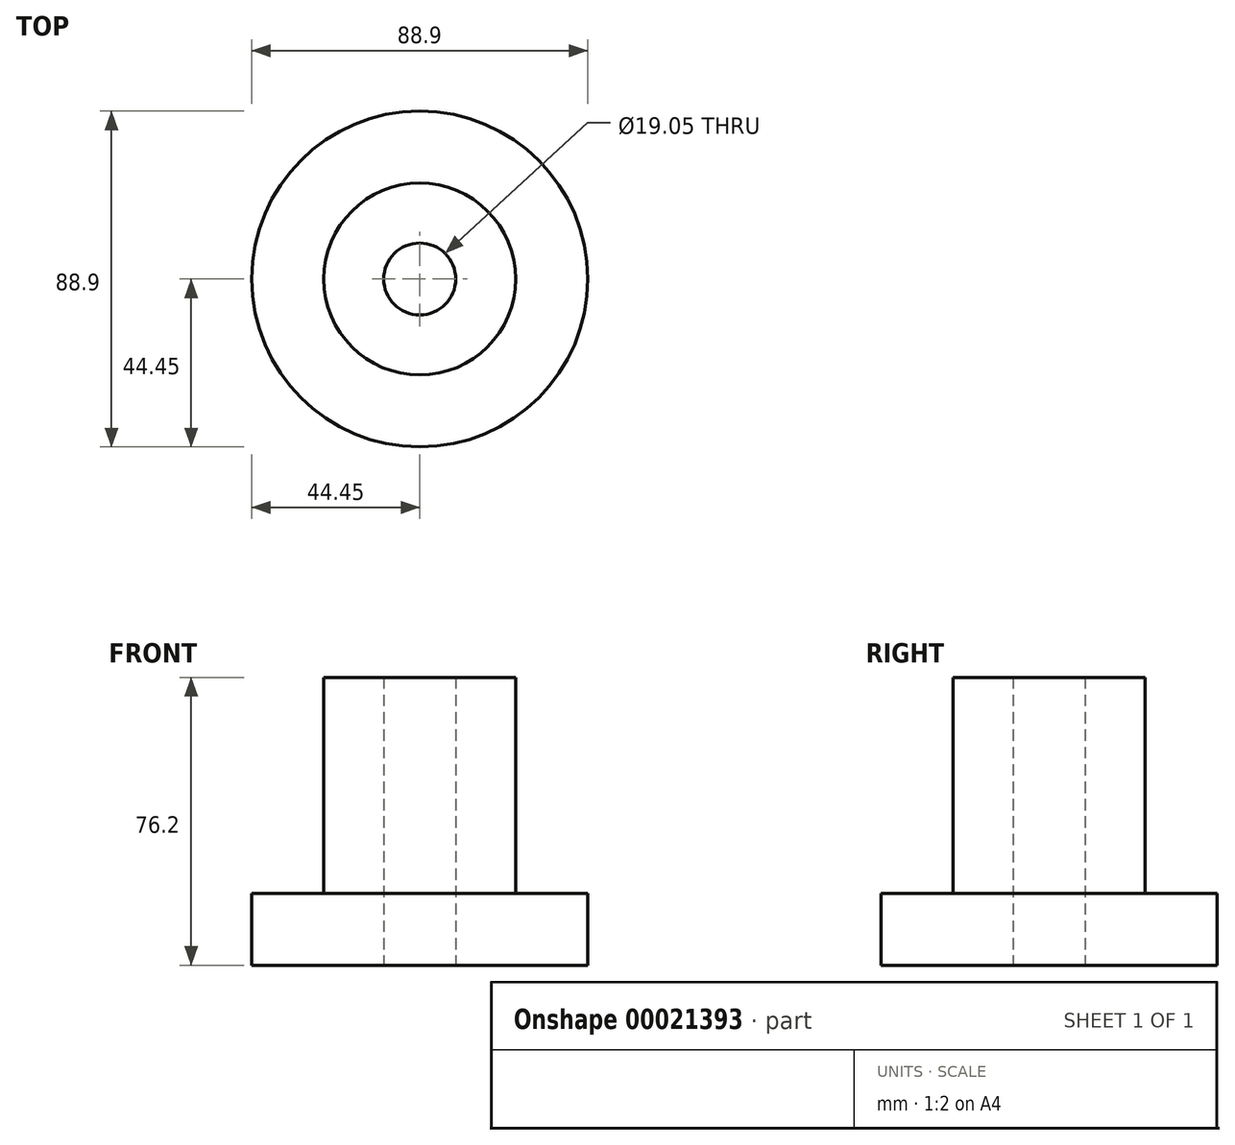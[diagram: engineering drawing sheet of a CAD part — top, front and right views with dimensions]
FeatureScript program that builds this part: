
annotation { "Feature Type Name" : "Feature", "Feature Type Description" : "" }
export const myFeature = defineFeature(function(context is Context, id is Id, definition is map)
    precondition{}
    {
        {
            var Q0;
            Q0=qCreatedBy(makeId("Front.planeOp"),FACE);
            var sketch = newSketch(context, id + "F0", { "sketchPlane" : qUnion([Q0])});
            skLineSegment(sketch, "E0", {"start": v(44.45, 0) * mm, "end": v(9.53, 0) * mm});
            skPoint(sketch, "E1.orphan", {"position": v(0, 95.25) * mm});
            skLineSegment(sketch, "E2.bottom", {"start": v(-44.45, 0) * mm, "end": v(-44.7, 0) * mm});
            skPoint(sketch, "E3.start.orphan", {"position": v(0, 72.96) * mm});
            skLineSegment(sketch, "E4", {"start": v(0, 90.32) * mm, "end": v(0, 83.59) * mm});
            skLineSegment(sketch, "E5.bottom", {"start": v(-44.45, 0) * mm, "end": v(0, 0) * mm});
            skLineSegment(sketch, "E5.top", {"start": v(-44.45, -19.05) * mm, "end": v(0, -19.05) * mm});
            skLineSegment(sketch, "E5.left", {"start": v(-44.45, 0) * mm, "end": v(-44.45, -19.05) * mm});
            skLineSegment(sketch, "E5.right", {"start": v(0, 0) * mm, "end": v(0, -19.05) * mm});
            skLineSegment(sketch, "E6.bottom", {"start": v(0, 0) * mm, "end": v(-25.4, 0) * mm});
            skLineSegment(sketch, "E6.top", {"start": v(0, 57.15) * mm, "end": v(-25.4, 57.15) * mm});
            skLineSegment(sketch, "E6.left", {"start": v(0, 0) * mm, "end": v(0, 57.15) * mm});
            skLineSegment(sketch, "E6.right", {"start": v(-25.4, 0) * mm, "end": v(-25.4, 57.15) * mm});
            skLineSegment(sketch, "E7.bottom", {"start": v(0, 57.15) * mm, "end": v(-19.05, 57.15) * mm});
            skLineSegment(sketch, "E7.top", {"start": v(0, 69.85) * mm, "end": v(-19.05, 69.85) * mm});
            skLineSegment(sketch, "E7.left", {"start": v(0, 57.15) * mm, "end": v(0, 69.85) * mm});
            skLineSegment(sketch, "E7.right", {"start": v(-19.05, 57.15) * mm, "end": v(-19.05, 69.85) * mm});
            skLineSegment(sketch, "E8.bottom", {"start": v(0, 69.85) * mm, "end": v(-9.53, 69.85) * mm});
            skLineSegment(sketch, "E9.left", {"start": v(0, 69.85) * mm, "end": v(0, -19.18) * mm});
            skLineSegment(sketch, "E10.left", {"start": v(0, 78.98) * mm, "end": v(0, -25.91) * mm});
            skLineSegment(sketch, "E11.bottom", {"start": v(0, 72.96) * mm, "end": v(9.53, 72.96) * mm});
            skLineSegment(sketch, "E11.top", {"start": v(0, -26.62) * mm, "end": v(9.53, -26.62) * mm});
            skLineSegment(sketch, "E11.left", {"start": v(0, 72.96) * mm, "end": v(0, -26.62) * mm});
            skLineSegment(sketch, "E11.right", {"start": v(9.53, 72.96) * mm, "end": v(9.53, -26.62) * mm});
            skLineSegment(sketch, "E12.trimOffspring", {"start": v(0, 0) * mm, "end": v(-44.45, 0) * mm});
            skSolve(sketch);
        }
        {
            var Q0;
            Q0=makeQuery(id+"F0.imprint","IMPRINT",FACE,{"disambiguationData":[TD([[makeQuery(id+"F0.imprint","IMPRINT",EDGE,{"derivedFrom":sQuery(id+"F0.wireOp",EDGE,"E6.top")}),1.0]])]});
            var Q1;
            {var subQ2=sQuery(id+"F0.wireOp",EDGE,"E7.bottom");Q1=makeQuery(id+"F0.imprint","IMPRINT",FACE,{"disambiguationData":[TD([[makeQuery(id+"F0.imprint","IMPRINT",EDGE,{"derivedFrom":subQ2}),-1.0]])]});}
            var Q2;
            {var subQ5=sQuery(id+"F0.wireOp",EDGE,"E5.top");Q2=makeQuery(id+"F0.imprint","IMPRINT",FACE,{"disambiguationData":[TD([[makeQuery(id+"F0.imprint","IMPRINT",EDGE,{"derivedFrom":subQ5}),1.0]])]});}
            var Q3;
            Q3=sQuery(id+"F0.wireOp",EDGE,"E4");
            revolve(context, id + "F1", {"entities" : qUnion([Q0, Q1, Q2]), "axis" : qUnion([Q3]), "revolveType" : RevolveType.FULL});
        }
        {
            var Q0;
            {var subQ6=sQuery(id+"F0.wireOp",EDGE,"E11.bottom");Q0=makeQuery(id+"F0.imprint","IMPRINT",FACE,{"disambiguationData":[TD([[makeQuery(id+"F0.imprint","IMPRINT",EDGE,{"derivedFrom":subQ6}),-1.0]])]});}
            var Q1;
            Q1=sQuery(id+"F0.wireOp",EDGE,"E4");
            revolve(context, id + "F2", {"operationType" : NewBodyOperationType.REMOVE, "entities" : qUnion([Q0]), "axis" : qUnion([Q1]), "revolveType" : RevolveType.FULL, "oppositeDirection" : true});
        }
    });
